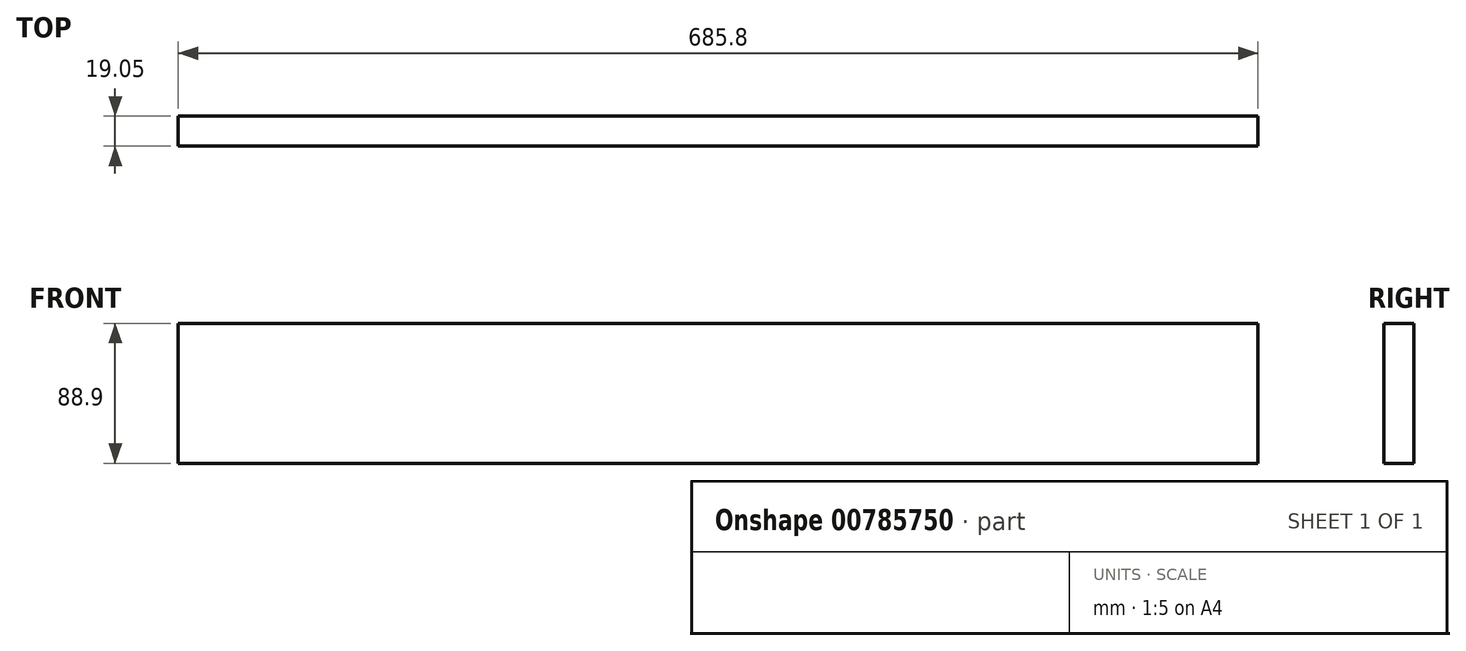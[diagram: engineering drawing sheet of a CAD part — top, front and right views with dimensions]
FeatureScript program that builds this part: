
annotation { "Feature Type Name" : "Feature", "Feature Type Description" : "" }
export const myFeature = defineFeature(function(context is Context, id is Id, definition is map)
    precondition{}
    {
        {
            var Q0;
            Q0=qCreatedBy(makeId("Top.planeOp"),FACE);
            var sketch = newSketch(context, id + "F0", { "sketchPlane" : qUnion([Q0])});
            skLineSegment(sketch, "E0.bottom", {"start": v(-330, 1.08) * mm, "end": v(355.8, 1.08) * mm});
            skLineSegment(sketch, "E0.top", {"start": v(-330, -17.97) * mm, "end": v(355.8, -17.97) * mm});
            skLineSegment(sketch, "E0.left", {"start": v(-330, 1.08) * mm, "end": v(-330, -17.97) * mm});
            skLineSegment(sketch, "E0.right", {"start": v(355.8, 1.08) * mm, "end": v(355.8, -17.97) * mm});
            skSolve(sketch);
        }
        {
            var Q0;
            Q0=makeQuery(id+"F0.imprint","IMPRINT",FACE,{"disambiguationData":[TD([[makeQuery(id+"F0.imprint","IMPRINT",EDGE,{"derivedFrom":sQuery(id+"F0.wireOp",EDGE,"E0.bottom")}),-1.0]])]});
            extrude(context, id + "F1", {"entities" : qUnion([Q0]), "oppositeDirection" : true, "depth" : 88.9 * mm, "offsetDistance" : 25.4 * mm});
        }
    });
